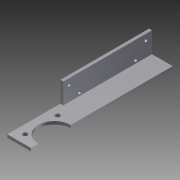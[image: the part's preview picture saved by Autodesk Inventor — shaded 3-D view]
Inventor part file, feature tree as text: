
AUTODESK INVENTOR PART (.ipt)
format: ipt  version: 2012 (Build 160160000, 160)  size: 94,720 bytes
history: native  units: in
note: dims shown in document units (in); Inventor stores cm internally (conversion verified against a paired STEP export)
features: other x3, sketch x2
ambient origin geometry x8: Origin, YZ Plane, XZ Plane, XY Plane, X Axis, Y Axis, Z Axis, Center Point
bodies: Solid1 (feature_tree)
feature tree (5):
  other  "8 ball corner L_MIR.ipt"
  other  "Solid1::8 ball corner L_MIR.ipt"
  sketch  "Sketch1"  dims[d0=0.3937in]
  sketch  "Sketch2"
  other  "TaggingFeature1"
